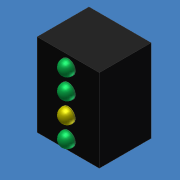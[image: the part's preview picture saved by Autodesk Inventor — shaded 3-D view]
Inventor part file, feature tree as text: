
AUTODESK INVENTOR PART (.ipt)
format: ipt  version: unknown  size: 220,160 bytes
history: native  units: mm (DEFAULTED — no unit token found)
features: extrude x5, fillet x4, sketch x2
ambient origin geometry x8: Origin, YZ Plane, XZ Plane, XY Plane, X Axis, Y Axis, Z Axis, Center Point
feature tree (11):
  extrude  "Extrusion1"  Depth=10.16mm
  sketch  "Sketch2"  dims[d2=6.35mm d3=0.0mm d4=1.27mm d5=1.778mm d6=1.016mm d7=0.0mm d8=0.889mm d12=40.0mm d14=2.54mm d15=10.0mm d17=25.4mm d19=1.016mm d20=0.0mm d21=0.889mm d22=1.016mm d23=0.0mm d24=0.889mm d25=1.016mm d26=0.0mm d27=0.889mm]
  extrude  "Extrusion2"  Depth=1.27mm
  fillet  "Fillet1"  Radius=1.778mm
  extrude  "Extrusion3"  Depth=1.016mm TaperAngle=0.0deg
  fillet  "Fillet2"  Radius=0.889mm
  extrude  "Extrusion4"  Depth=40.0mm
  fillet  "Fillet3"  Radius=1.016mm
  extrude  "Extrusion5"  Depth=0.889mm
  fillet  "Fillet4"  Radius=1.016mm
  sketch  "Sketch1"  dims[d0=7.62mm d1=10.16mm]
